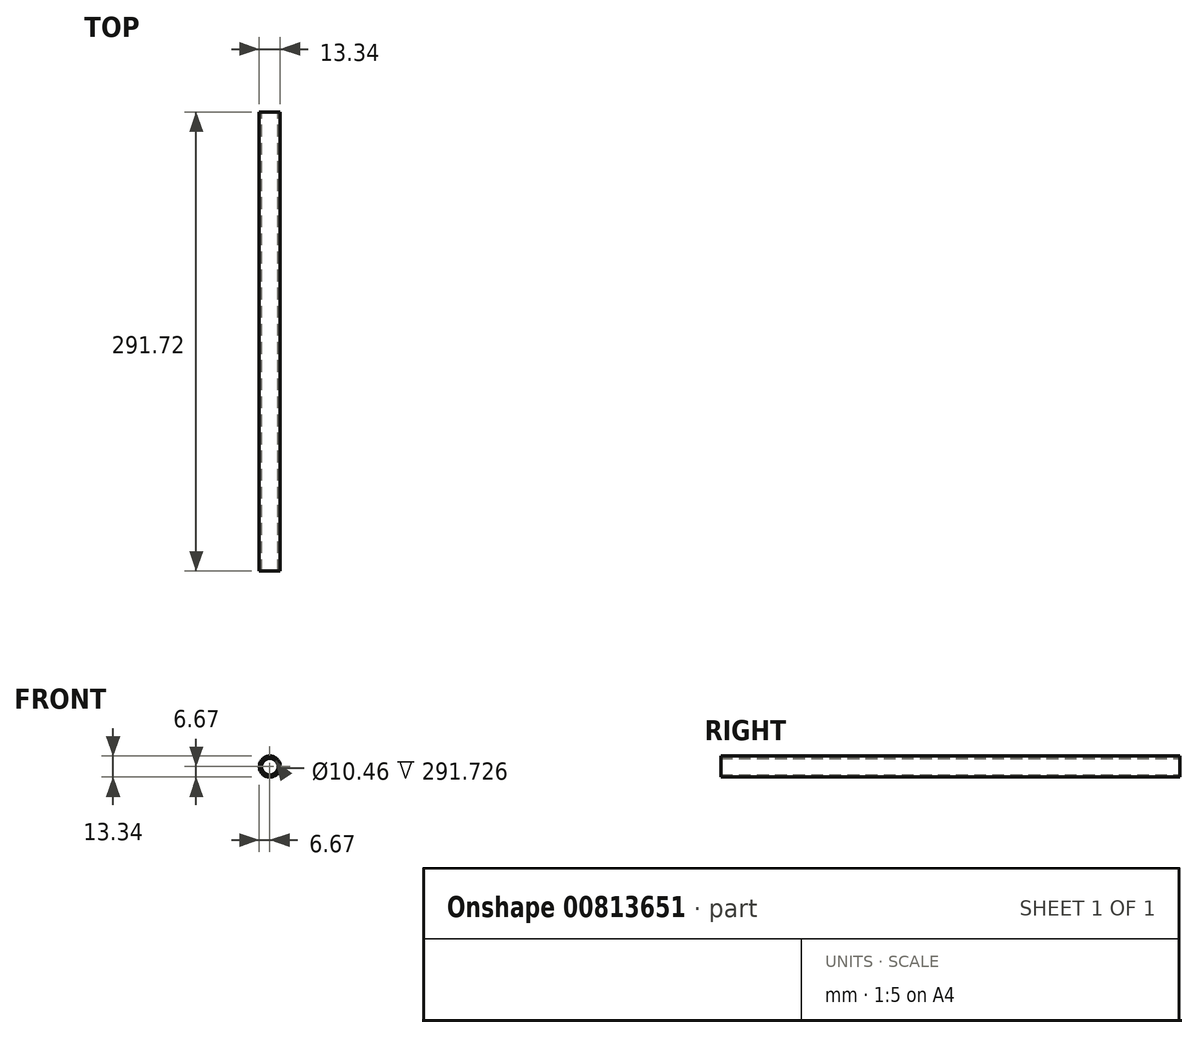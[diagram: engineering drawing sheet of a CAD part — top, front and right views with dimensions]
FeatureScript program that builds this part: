
annotation { "Feature Type Name" : "Feature", "Feature Type Description" : "" }
export const myFeature = defineFeature(function(context is Context, id is Id, definition is map)
    precondition{}
    {
        {
            var Q0;
            Q0=qCreatedBy(makeId("Front.planeOp"),FACE);
            var sketch = newSketch(context, id + "F0", { "sketchPlane" : qUnion([Q0])});
            skCircle(sketch, "E0", {"center": v(0, 0) * mm, "radius": 6.67 * mm});
            skCircle(sketch, "E1", {"center": v(0, 0) * mm, "radius": 5.23 * mm});
            skSolve(sketch);
        }
        {
            var Q0;
            Q0 = qSketchRegion(id + "F0", true);
            extrude(context, id + "F1", {"entities" : qUnion([Q0]), "endBound" : BoundingType.SYMMETRIC, "depth" : 291.73 * mm, "offsetDistance" : 25.4 * mm});
        }
    });
